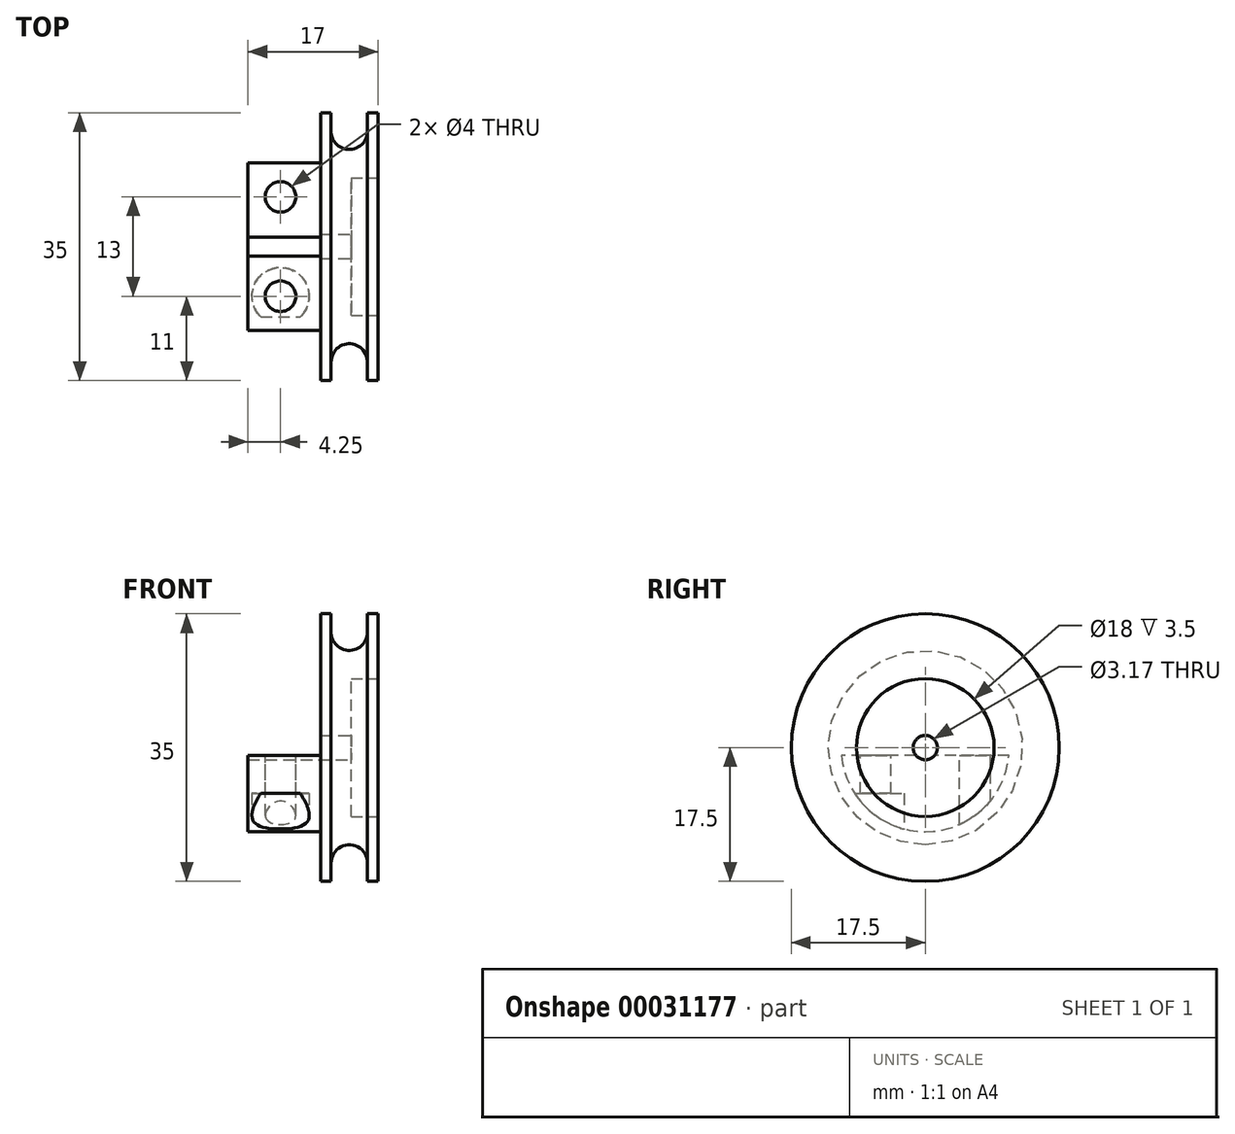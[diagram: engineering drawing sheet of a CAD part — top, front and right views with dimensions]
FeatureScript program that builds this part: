
annotation { "Feature Type Name" : "Feature", "Feature Type Description" : "" }
export const myFeature = defineFeature(function(context is Context, id is Id, definition is map)
    precondition{}
    {
        {
            var Q0;
            Q0=qCreatedBy(makeId("Front.planeOp"),FACE);
            var sketch = newSketch(context, id + "F0", { "sketchPlane" : qUnion([Q0])});
            skLineSegment(sketch, "E0", {"start": v(0, 0) * mm, "end": v(0, 17.5) * mm});
            skLineSegment(sketch, "E1", {"start": v(0, 17.5) * mm, "end": v(1.37, 17.5) * mm});
            skLineSegment(sketch, "E2", {"start": v(6.13, 17.5) * mm, "end": v(7.5, 17.5) * mm});
            skLineSegment(sketch, "E3", {"start": v(7.5, 17.5) * mm, "end": v(7.5, 9) * mm});
            skLineSegment(sketch, "E4", {"start": v(4, 0) * mm, "end": v(0, 0) * mm});
            skLineSegment(sketch, "E5", {"start": v(7.5, 9) * mm, "end": v(4, 9) * mm});
            skLineSegment(sketch, "E6", {"start": v(4, 9) * mm, "end": v(4, 0) * mm});
            skPoint(sketch, "E7.orphan", {"position": v(7.5, 0) * mm});
            skLineSegment(sketch, "E8", {"start": v(1.37, 17.5) * mm, "end": v(1.37, 15.08) * mm});
            skLineSegment(sketch, "E9", {"start": v(6.13, 17.5) * mm, "end": v(6.13, 15.08) * mm});
            skArc(sketch, "E10", {"start": v(1.37, 15.08) * mm, "mid": v(3.75, 12.7) * mm, "end": v(6.13, 15.08) * mm});
            skSolve(sketch);
        }
        {
            var Q0;
            Q0=qSketchRegion(id+"F0",true);
            var Q1;
            Q1=sQuery(id+"F0.wireOp",EDGE,"E4");
            revolve(context, id + "F1", {"entities" : qUnion([Q0]), "axis" : qUnion([Q1]), "revolveType" : RevolveType.FULL});
        }
        {
            var Q0;
            Q0=makeQuery(id+"F1.opRevolve","SWEPT_FACE",FACE,{"disambiguationData":[OSD([sQuery(id+"F0.wireOp",EDGE,"E3")])]});
            var sketch = newSketch(context, id + "F2", { "sketchPlane" : qUnion([Q0])});
            skCircle(sketch, "E11", {"center": v(0, 0) * mm, "radius": 1.59 * mm});
            skCircle(sketch, "E12", {"center": v(0, 0) * mm, "radius": 9.53 * mm, "construction": true});
            skCircle(sketch, "E13", {"center": v(0, 9.53) * mm, "radius": 2.5 * mm, "construction": true});
            skCircle(sketch, "E14", {"center": v(9.53, 0) * mm, "radius": 2.5 * mm, "construction": true});
            skCircle(sketch, "E15", {"center": v(0, -9.53) * mm, "radius": 2.5 * mm, "construction": true});
            skCircle(sketch, "E16", {"center": v(-9.53, 0) * mm, "radius": 2.5 * mm, "construction": true});
            skSolve(sketch);
        }
        {
            var Q0;
            Q0=qSketchRegion(id+"F2",true);
            extrude(context, id + "F3", {"entities" : qUnion([Q0]), "operationType" : NewBodyOperationType.REMOVE, "endBound" : BoundingType.THROUGH_ALL, "oppositeDirection" : true, "depth" : 25 * mm});
        }
        {
            var Q0;
            Q0=makeQuery(id+"F1.opRevolve","SWEPT_FACE",FACE,{"disambiguationData":[OSD([sQuery(id+"F0.wireOp",EDGE,"E0")])]});
            var sketch = newSketch(context, id + "F4", { "sketchPlane" : qUnion([Q0])});
            skArc(sketch, "E17", {"start": v(-10.95, -1) * mm, "mid": v(0, -11) * mm, "end": v(10.95, -1) * mm});
            skLineSegment(sketch, "E18.bottom", {"start": v(3.51, 15.8) * mm, "end": v(7.51, 15.8) * mm, "construction": true});
            skLineSegment(sketch, "E18.top", {"start": v(3.51, -15.8) * mm, "end": v(7.51, -15.8) * mm, "construction": true});
            skLineSegment(sketch, "E18.left", {"start": v(3.51, 15.8) * mm, "end": v(3.51, -15.8) * mm, "construction": true});
            skLineSegment(sketch, "E18.right", {"start": v(7.51, 15.8) * mm, "end": v(7.51, -15.8) * mm, "construction": true});
            skLineSegment(sketch, "E19.bottom", {"start": v(-7.51, 13.38) * mm, "end": v(-3.51, 13.38) * mm, "construction": true});
            skLineSegment(sketch, "E19.top", {"start": v(-7.51, -13.38) * mm, "end": v(-3.51, -13.38) * mm, "construction": true});
            skLineSegment(sketch, "E19.left", {"start": v(-7.51, 13.38) * mm, "end": v(-7.51, -13.38) * mm, "construction": true});
            skLineSegment(sketch, "E19.right", {"start": v(-3.51, 13.38) * mm, "end": v(-3.51, -13.38) * mm, "construction": true});
            skLineSegment(sketch, "E20", {"start": v(-3.51, 0) * mm, "end": v(0, 0) * mm, "construction": true});
            skLineSegment(sketch, "E21", {"start": v(3.51, 0) * mm, "end": v(0, 0) * mm, "construction": true});
            skLineSegment(sketch, "E22", {"start": v(-3.51, 13.38) * mm, "end": v(-1.51, 13.38) * mm, "construction": true});
            skLineSegment(sketch, "E23", {"start": v(-10.95, -1) * mm, "end": v(-1.23, -1) * mm});
            skArc(sketch, "E24", {"start": v(-1.23, -1) * mm, "mid": v(0, -1.59) * mm, "end": v(1.23, -1) * mm});
            skLineSegment(sketch, "E25.trimOffspring", {"start": v(1.23, -1) * mm, "end": v(10.95, -1) * mm});
            skSolve(sketch);
        }
        {
            var Q0;
            Q0 = qSketchRegion(id + "F4", true);
            extrude(context, id + "F5", {"entities" : qUnion([Q0]), "operationType" : NewBodyOperationType.ADD, "depth" : (8.5 + 1) * mm});
        }
        {
            var Q0;
            Q0=makeQuery(id+"F5.opExtrude","SWEPT_FACE",FACE,{"disambiguationData":[OSD([sQuery(id+"F4.wireOp",EDGE,"E23")])]});
            var sketch = newSketch(context, id + "F6", { "sketchPlane" : qUnion([Q0])});
            skCircle(sketch, "E26", {"center": v(-5.25, 6.5) * mm, "radius": 2 * mm});
            skCircle(sketch, "E27", {"center": v(-5.25, -6.5) * mm, "radius": 2 * mm});
            skLineSegment(sketch, "E28", {"start": v(-5.25, 6.5) * mm, "end": v(-5.25, -6.5) * mm, "construction": true});
            skLineSegment(sketch, "E29", {"start": v(0, 0) * mm, "end": v(-5.25, 0) * mm, "construction": true});
            skSolve(sketch);
        }
        {
            var Q0;
            Q0 = qSketchRegion(id + "F6", true);
            extrude(context, id + "F7", {"entities" : qUnion([Q0]), "operationType" : NewBodyOperationType.REMOVE, "endBound" : BoundingType.THROUGH_ALL, "oppositeDirection" : true, "depth" : 25 * mm});
        }
        {
            var Q0;
            Q0=makeQuery(id+"F5.opExtrude","SWEPT_FACE",FACE,{"disambiguationData":[OSD([sQuery(id+"F4.wireOp",EDGE,"E25.trimOffspring")])]});
            cPlane(context, id + "F8", {"entities" : qUnion([Q0]), "cplaneType" : CPlaneType.OFFSET, "offset" : 10 * mm, "oppositeDirection" : true, "width" : 150 * mm, "height" : 150 * mm});
        }
        {
            var Q0;
            Q0=qCreatedBy(id+"F8.planeOp",FACE);
            var sketch = newSketch(context, id + "F9", { "sketchPlane" : qUnion([Q0])});
            skCircle(sketch, "E30", {"center": v(-5.25, -6.5) * mm, "radius": 3.75 * mm});
            skSolve(sketch);
        }
        {
            var Q0;
            Q0 = qSketchRegion(id + "F9", true);
            var Q1;
            Q1=makeQuery(id+"F5.opExtrude","SWEPT_FACE",FACE,{"disambiguationData":[OSD([sQuery(id+"F4.wireOp",EDGE,"E25.trimOffspring")])]});
            extrude(context, id + "F10", {"entities" : qUnion([Q0]), "operationType" : NewBodyOperationType.REMOVE, "endBoundEntityFace" : qUnion([Q1]), "depth" : 5 * mm});
        }
    });
